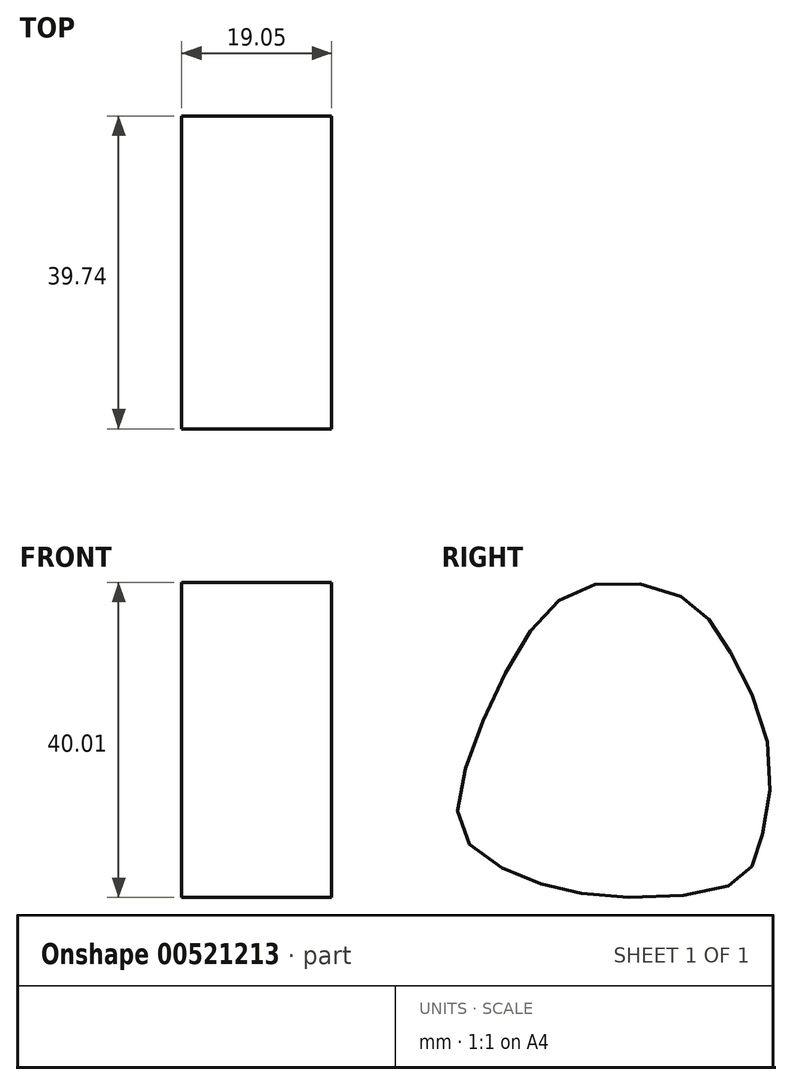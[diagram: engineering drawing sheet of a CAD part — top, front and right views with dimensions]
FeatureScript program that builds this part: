
annotation { "Feature Type Name" : "Feature", "Feature Type Description" : "" }
export const myFeature = defineFeature(function(context is Context, id is Id, definition is map)
    precondition{}
    {
        {
            var Q0;
            Q0=qCreatedBy(makeId("Right.planeOp"),FACE);
            var sketch = newSketch(context, id + "F0", { "sketchPlane" : qUnion([Q0])});
            skFitSpline(sketch, "E0", {"points": [v(8.36, 19.67) * mm, v(-3.24, 21.01) * mm, v(-11.1, 14.76) * mm, v(-18.28, 0) * mm, v(-19.37, -10.54) * mm, v(-11.34, -16.14) * mm, v(0, -18.48) * mm, v(15.08, -16.8) * mm, v(18.24, -12.33) * mm, v(19.53, 0) * mm, v(14.15, 13.38) * mm, v(8.36, 19.67) * mm]});
            skSolve(sketch);
        }
        {
            var Q0;
            Q0 = qSketchRegion(id + "F0", true);
            extrude(context, id + "F1", {"entities" : qUnion([Q0]), "depth" : 19.05 * mm, "offsetDistance" : 25.4 * mm});
        }
    });
